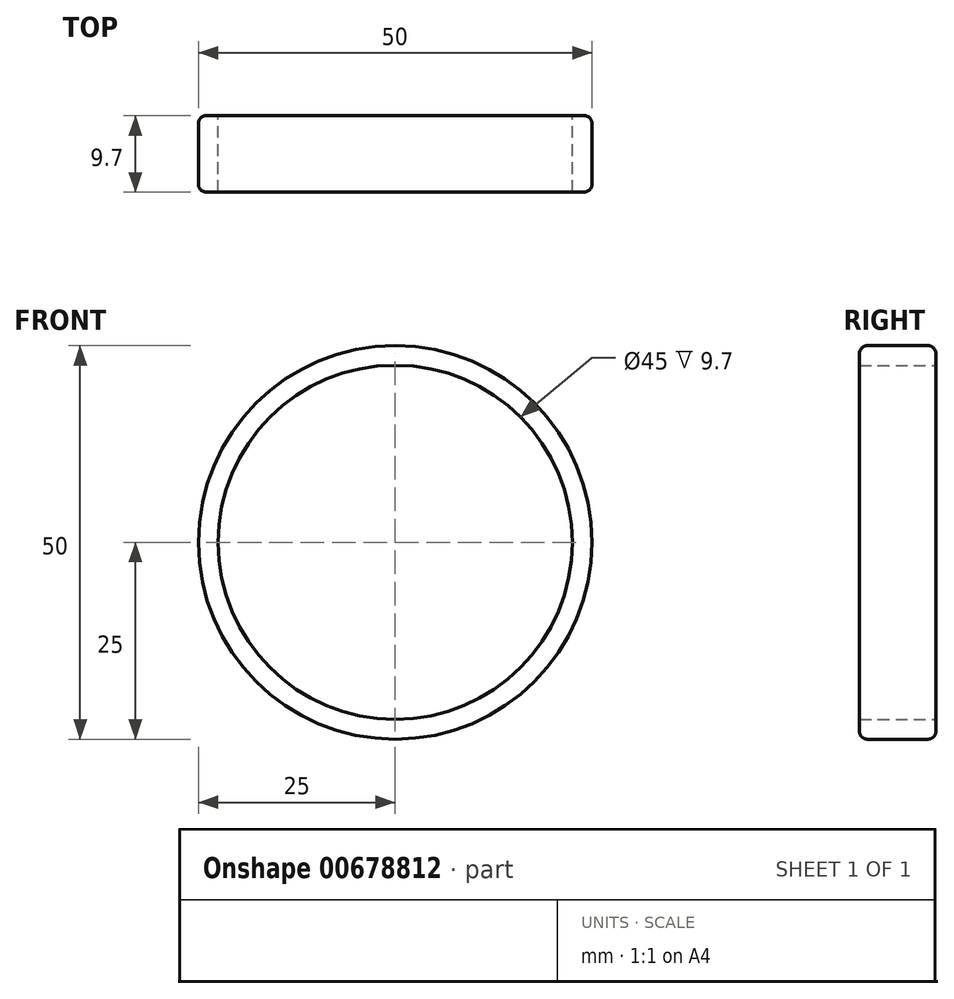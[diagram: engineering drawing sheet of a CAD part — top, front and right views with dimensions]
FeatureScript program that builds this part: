
annotation { "Feature Type Name" : "Feature", "Feature Type Description" : "" }
export const myFeature = defineFeature(function(context is Context, id is Id, definition is map)
    precondition{}
    {
        {
            var Q0;
            Q0=qCreatedBy(makeId("Front.planeOp"),FACE);
            var sketch = newSketch(context, id + "F0", { "sketchPlane" : qUnion([Q0])});
            skCircle(sketch, "E0", {"center": v(0, 0) * mm, "radius": 22.5 * mm});
            skCircle(sketch, "E1", {"center": v(0, 0) * mm, "radius": 25 * mm});
            skSolve(sketch);
        }
        {
            var Q0;
            Q0=makeQuery(id+"F0.imprint","IMPRINT",FACE,{"disambiguationData":[TD([[makeQuery(id+"F0.imprint","IMPRINT",EDGE,{"derivedFrom":sQuery(id+"F0.wireOp",EDGE,"E0")}),-1.0]])]});
            extrude(context, id + "F1", {"entities" : qUnion([Q0]), "depth" : 9.7 * mm, "offsetDistance" : 25 * mm});
        }
        {
            var Q0;
            Q0=makeQuery(id+"F1.opExtrude","CAP_EDGE",EDGE,{"disambiguationData":[OSD([sQuery(id+"F0.wireOp",EDGE,"E1")])],"isStart":false});
            var Q1;
            Q1=makeQuery(id+"F1.opExtrude","SWEPT_FACE",FACE,{"disambiguationData":[OSD([sQuery(id+"F0.wireOp",EDGE,"E1")])]});
            fillet(context, id + "F2", {"entities" : qUnion([Q0, Q1]), "radius" : 1 * mm, "tangentPropagation" : true, "allowEdgeOverflow" : false});
        }
    });
